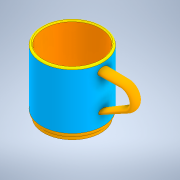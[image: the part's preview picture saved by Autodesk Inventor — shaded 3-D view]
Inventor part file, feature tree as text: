
AUTODESK INVENTOR PART (.ipt)
format: ipt  version: 2022.5 (Build 265521000, 521)  size: 248,320 bytes
history: native  units: in
note: dims shown in document units (in); Inventor stores cm internally (conversion verified against a paired STEP export)
features: sketch x11, other x2, plane x2, revolve x1, shell x1, loft x1, fillet x1, extrude x1
ambient origin geometry x8: Origin, YZ Plane, XZ Plane, XY Plane, X Axis, Y Axis, Z Axis, Center Point
bodies: Solid1 (feature_tree)
feature tree (20):
  sketch  "Sketch1"  dims[d0=2.7559in d1=1.378in d2=2.5591in]
  revolve  "Revolution1"  [1 undecoded]
  shell  "Shell1"  Thickness=2.5591in
  sketch  "Sketch3"  dims[d24=0.0in d25=90.0deg d26=0.0in d27=90.0deg]
  sketch  "Sketch4"  dims[d28=0.0in d29=90.0deg]
  other  "Work Point1"
  plane  "Work Plane1"
  sketch  "Sketch5"  dims[d30=0.0787in]
  sketch  "Sketch6"  dims[d31=2.5591in]
  sketch  "Sketch7"  dims[d32=2.4409in]
  sketch  "Sketch8"  dims[d33=0.1181in d34=0.0in]
  other  "Work Point2"
  plane  "Work Plane2"
  sketch  "Sketch9"  dims[d35=0.0197in]
  sketch  "Sketch10"  dims[d36=0.0344in]
  loft  "Loft1"
  fillet  "Fillet1"  Radius=0.1181in
  extrude  "Extrusion1"  TaperAngle=0.0deg  [1 undecoded]
  sketch  "Sketch2"  dims[d3=1.2795in d6=90.0deg d7=0.1181in]
  sketch  "Sketch11"
note: 2 required parameter values undecoded (feature->parameter linkage not recoverable at this tier; creation-order binding heuristic only, values carry confidence <= 0.55)